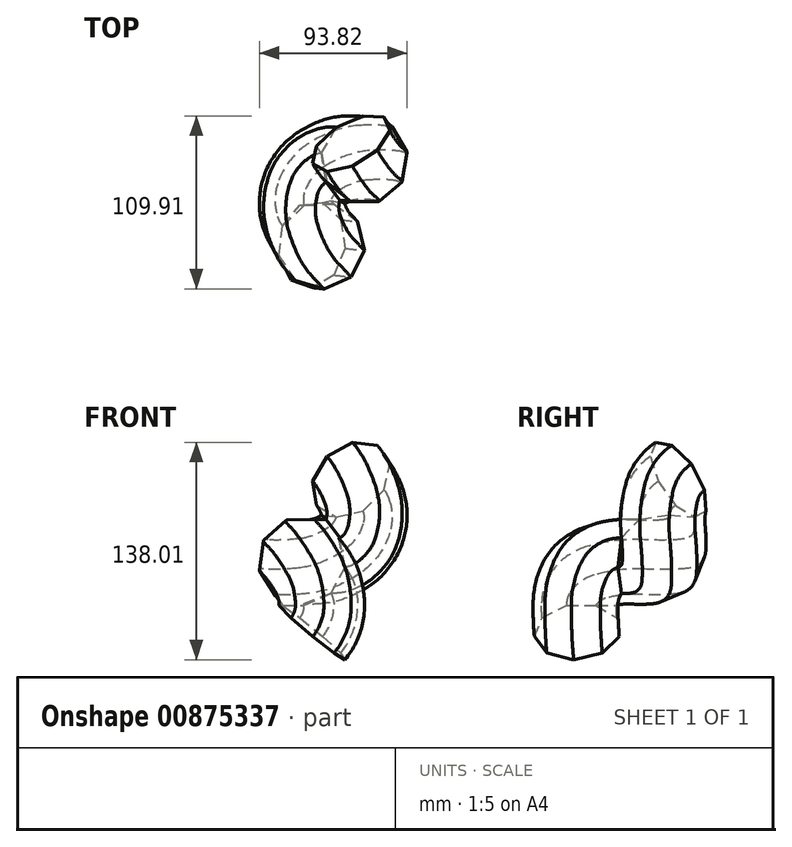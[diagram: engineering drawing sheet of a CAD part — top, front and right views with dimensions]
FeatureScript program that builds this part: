
annotation { "Feature Type Name" : "Feature", "Feature Type Description" : "" }
export const myFeature = defineFeature(function(context is Context, id is Id, definition is map)
    precondition{}
    {
        {
            var Q0;
            Q0=qCreatedBy(makeId("Top.planeOp"),FACE);
            var sketch = newSketch(context, id + "F0", { "sketchPlane" : qUnion([Q0])});
            skCircle(sketch, "E0.cCircle", {"center": v(0, 0) * mm, "radius": 25.92 * mm, "construction": true});
            skLineSegment(sketch, "E0.0", {"start": v(27.4, -3.23) * mm, "end": v(18.91, -20.08) * mm});
            skLineSegment(sketch, "E0.1", {"start": v(18.91, -20.08) * mm, "end": v(1.58, -27.54) * mm});
            skLineSegment(sketch, "E0.2", {"start": v(1.58, -27.54) * mm, "end": v(-16.5, -22.11) * mm});
            skLineSegment(sketch, "E0.3", {"start": v(-16.5, -22.11) * mm, "end": v(-26.85, -6.33) * mm});
            skLineSegment(sketch, "E0.4", {"start": v(-26.85, -6.33) * mm, "end": v(-24.64, 12.4) * mm});
            skLineSegment(sketch, "E0.5", {"start": v(-24.64, 12.4) * mm, "end": v(-10.9, 25.34) * mm});
            skLineSegment(sketch, "E0.6", {"start": v(-10.9, 25.34) * mm, "end": v(7.94, 26.42) * mm});
            skLineSegment(sketch, "E0.7", {"start": v(7.94, 26.42) * mm, "end": v(23.06, 15.14) * mm});
            skLineSegment(sketch, "E0.8", {"start": v(23.06, 15.14) * mm, "end": v(27.4, -3.23) * mm});
            skPoint(sketch, "E0.0.midPoint", {"position": v(23.15, -11.66) * mm});
            skSolve(sketch);
        }
        {
            var Q0;
            Q0=makeQuery(id+"F0.imprint","IMPRINT",FACE,{"disambiguationData":[TD([[makeQuery(id+"F0.imprint","IMPRINT",EDGE,{"derivedFrom":sQuery(id+"F0.wireOp",EDGE,"E0.0")}),-1.0]])]});
            var Q1;
            Q1=sQuery(id+"F0.wireOp",EDGE,"E0.4");
            revolve(context, id + "F1", {"surfaceOperationType" : NewSurfaceOperationType.NEW, "entities" : qUnion([Q0]), "axis" : qUnion([Q1]), "revolveType" : RevolveType.ONE_DIRECTION, "angle" : 40 * degree});
        }
        {
            var Q0;
            Q0=makeQuery(id+"F1.opRevolve","CAP_FACE",FACE,{"disambiguationData":[OSD([sQuery(id+"F0.wireOp",EDGE,"E0.0"),sQuery(id+"F0.wireOp",EDGE,"E0.1"),sQuery(id+"F0.wireOp",EDGE,"E0.2"),sQuery(id+"F0.wireOp",EDGE,"E0.3"),sQuery(id+"F0.wireOp",EDGE,"E0.4"),sQuery(id+"F0.wireOp",EDGE,"E0.5"),sQuery(id+"F0.wireOp",EDGE,"E0.6"),sQuery(id+"F0.wireOp",EDGE,"E0.7"),sQuery(id+"F0.wireOp",EDGE,"E0.8")])],"isStart":true});
            var Q1;
            Q1=makeQuery(id+"F1.opRevolve","CAP_EDGE",EDGE,{"disambiguationData":[OSD([sQuery(id+"F0.wireOp",EDGE,"E0.5")])],"isStart":true});
            revolve(context, id + "F2", {"operationType" : NewBodyOperationType.ADD, "surfaceOperationType" : NewSurfaceOperationType.NEW, "entities" : qUnion([Q0]), "axis" : qUnion([Q1]), "revolveType" : RevolveType.ONE_DIRECTION, "oppositeDirection" : true, "angle" : 40 * degree});
        }
        {
            var Q0;
            Q0=makeQuery(id+"F2.opRevolve","CAP_FACE",FACE,{"disambiguationData":[OSD([sQuery(id+"F0.wireOp",EDGE,"E0.0"),sQuery(id+"F0.wireOp",EDGE,"E0.1"),sQuery(id+"F0.wireOp",EDGE,"E0.2"),sQuery(id+"F0.wireOp",EDGE,"E0.3"),sQuery(id+"F0.wireOp",EDGE,"E0.4"),sQuery(id+"F0.wireOp",EDGE,"E0.5"),sQuery(id+"F0.wireOp",EDGE,"E0.6"),sQuery(id+"F0.wireOp",EDGE,"E0.7"),sQuery(id+"F0.wireOp",EDGE,"E0.8")])],"isStart":false});
            var Q1;
            Q1=makeQuery(id+"F2.opRevolve","CAP_EDGE",EDGE,{"disambiguationData":[OSD([sQuery(id+"F0.wireOp",EDGE,"E0.6")])],"isStart":false});
            revolve(context, id + "F3", {"operationType" : NewBodyOperationType.ADD, "surfaceOperationType" : NewSurfaceOperationType.NEW, "entities" : qUnion([Q0]), "axis" : qUnion([Q1]), "revolveType" : RevolveType.ONE_DIRECTION, "oppositeDirection" : true, "angle" : 40 * degree});
        }
        {
            var Q0;
            Q0=makeQuery(id+"F3.opRevolve","CAP_FACE",FACE,{"disambiguationData":[OSD([sQuery(id+"F0.wireOp",EDGE,"E0.0"),sQuery(id+"F0.wireOp",EDGE,"E0.1"),sQuery(id+"F0.wireOp",EDGE,"E0.2"),sQuery(id+"F0.wireOp",EDGE,"E0.3"),sQuery(id+"F0.wireOp",EDGE,"E0.4"),sQuery(id+"F0.wireOp",EDGE,"E0.5"),sQuery(id+"F0.wireOp",EDGE,"E0.6"),sQuery(id+"F0.wireOp",EDGE,"E0.7"),sQuery(id+"F0.wireOp",EDGE,"E0.8")])],"isStart":false});
            var Q1;
            Q1=makeQuery(id+"F3.opRevolve","CAP_EDGE",EDGE,{"disambiguationData":[OSD([sQuery(id+"F0.wireOp",EDGE,"E0.7")])],"isStart":false});
            revolve(context, id + "F4", {"operationType" : NewBodyOperationType.ADD, "surfaceOperationType" : NewSurfaceOperationType.NEW, "entities" : qUnion([Q0]), "axis" : qUnion([Q1]), "revolveType" : RevolveType.ONE_DIRECTION, "oppositeDirection" : true, "angle" : 40 * degree});
        }
        {
            var Q0;
            Q0=makeQuery(id+"F4.opRevolve","CAP_FACE",FACE,{"disambiguationData":[OSD([sQuery(id+"F0.wireOp",EDGE,"E0.0"),sQuery(id+"F0.wireOp",EDGE,"E0.1"),sQuery(id+"F0.wireOp",EDGE,"E0.2"),sQuery(id+"F0.wireOp",EDGE,"E0.3"),sQuery(id+"F0.wireOp",EDGE,"E0.4"),sQuery(id+"F0.wireOp",EDGE,"E0.5"),sQuery(id+"F0.wireOp",EDGE,"E0.6"),sQuery(id+"F0.wireOp",EDGE,"E0.7"),sQuery(id+"F0.wireOp",EDGE,"E0.8")])],"isStart":false});
            var Q1;
            Q1=makeQuery(id+"F4.opRevolve","CAP_EDGE",EDGE,{"disambiguationData":[OSD([sQuery(id+"F0.wireOp",EDGE,"E0.8")])],"isStart":false});
            revolve(context, id + "F5", {"operationType" : NewBodyOperationType.ADD, "surfaceOperationType" : NewSurfaceOperationType.NEW, "entities" : qUnion([Q0]), "axis" : qUnion([Q1]), "revolveType" : RevolveType.ONE_DIRECTION, "oppositeDirection" : true, "angle" : 40 * degree});
        }
        {
            var Q0;
            Q0=makeQuery(id+"F5.opRevolve","CAP_FACE",FACE,{"disambiguationData":[OSD([sQuery(id+"F0.wireOp",EDGE,"E0.0"),sQuery(id+"F0.wireOp",EDGE,"E0.1"),sQuery(id+"F0.wireOp",EDGE,"E0.2"),sQuery(id+"F0.wireOp",EDGE,"E0.3"),sQuery(id+"F0.wireOp",EDGE,"E0.4"),sQuery(id+"F0.wireOp",EDGE,"E0.5"),sQuery(id+"F0.wireOp",EDGE,"E0.6"),sQuery(id+"F0.wireOp",EDGE,"E0.7"),sQuery(id+"F0.wireOp",EDGE,"E0.8")])],"isStart":false});
            var Q1;
            Q1=makeQuery(id+"F5.opRevolve","CAP_EDGE",EDGE,{"disambiguationData":[OSD([sQuery(id+"F0.wireOp",EDGE,"E0.0")])],"isStart":false});
            revolve(context, id + "F6", {"operationType" : NewBodyOperationType.ADD, "surfaceOperationType" : NewSurfaceOperationType.NEW, "entities" : qUnion([Q0]), "axis" : qUnion([Q1]), "revolveType" : RevolveType.ONE_DIRECTION, "oppositeDirection" : true, "angle" : 40 * degree});
        }
        {
            var Q0;
            Q0=makeQuery(id+"F6.opRevolve","CAP_FACE",FACE,{"disambiguationData":[OSD([sQuery(id+"F0.wireOp",EDGE,"E0.0"),sQuery(id+"F0.wireOp",EDGE,"E0.1"),sQuery(id+"F0.wireOp",EDGE,"E0.2"),sQuery(id+"F0.wireOp",EDGE,"E0.3"),sQuery(id+"F0.wireOp",EDGE,"E0.4"),sQuery(id+"F0.wireOp",EDGE,"E0.5"),sQuery(id+"F0.wireOp",EDGE,"E0.6"),sQuery(id+"F0.wireOp",EDGE,"E0.7"),sQuery(id+"F0.wireOp",EDGE,"E0.8")])],"isStart":false});
            var Q1;
            Q1=makeQuery(id+"F6.opRevolve","CAP_EDGE",EDGE,{"disambiguationData":[OSD([sQuery(id+"F0.wireOp",EDGE,"E0.1")])],"isStart":false});
            revolve(context, id + "F7", {"operationType" : NewBodyOperationType.ADD, "surfaceOperationType" : NewSurfaceOperationType.NEW, "entities" : qUnion([Q0]), "axis" : qUnion([Q1]), "revolveType" : RevolveType.ONE_DIRECTION, "oppositeDirection" : true, "angle" : 40 * degree});
        }
        {
            var Q0;
            Q0=makeQuery(id+"F7.opRevolve","CAP_FACE",FACE,{"disambiguationData":[OSD([sQuery(id+"F0.wireOp",EDGE,"E0.0"),sQuery(id+"F0.wireOp",EDGE,"E0.1"),sQuery(id+"F0.wireOp",EDGE,"E0.2"),sQuery(id+"F0.wireOp",EDGE,"E0.3"),sQuery(id+"F0.wireOp",EDGE,"E0.4"),sQuery(id+"F0.wireOp",EDGE,"E0.5"),sQuery(id+"F0.wireOp",EDGE,"E0.6"),sQuery(id+"F0.wireOp",EDGE,"E0.7"),sQuery(id+"F0.wireOp",EDGE,"E0.8")])],"isStart":false});
            var Q1;
            Q1=makeQuery(id+"F7.opRevolve","CAP_EDGE",EDGE,{"disambiguationData":[OSD([sQuery(id+"F0.wireOp",EDGE,"E0.2")])],"isStart":false});
            revolve(context, id + "F8", {"operationType" : NewBodyOperationType.ADD, "surfaceOperationType" : NewSurfaceOperationType.NEW, "entities" : qUnion([Q0]), "axis" : qUnion([Q1]), "revolveType" : RevolveType.ONE_DIRECTION, "oppositeDirection" : true, "angle" : 40 * degree});
        }
        {
            var Q0;
            Q0=makeQuery(id+"F8.opRevolve","CAP_FACE",FACE,{"disambiguationData":[OSD([sQuery(id+"F0.wireOp",EDGE,"E0.0"),sQuery(id+"F0.wireOp",EDGE,"E0.1"),sQuery(id+"F0.wireOp",EDGE,"E0.2"),sQuery(id+"F0.wireOp",EDGE,"E0.3"),sQuery(id+"F0.wireOp",EDGE,"E0.4"),sQuery(id+"F0.wireOp",EDGE,"E0.5"),sQuery(id+"F0.wireOp",EDGE,"E0.6"),sQuery(id+"F0.wireOp",EDGE,"E0.7"),sQuery(id+"F0.wireOp",EDGE,"E0.8")])],"isStart":false});
            var Q1;
            Q1=makeQuery(id+"F8.opRevolve","CAP_EDGE",EDGE,{"disambiguationData":[OSD([sQuery(id+"F0.wireOp",EDGE,"E0.3")])],"isStart":false});
            revolve(context, id + "F9", {"operationType" : NewBodyOperationType.ADD, "surfaceOperationType" : NewSurfaceOperationType.NEW, "entities" : qUnion([Q0]), "axis" : qUnion([Q1]), "revolveType" : RevolveType.ONE_DIRECTION, "oppositeDirection" : true, "angle" : 40 * degree});
        }
    });
